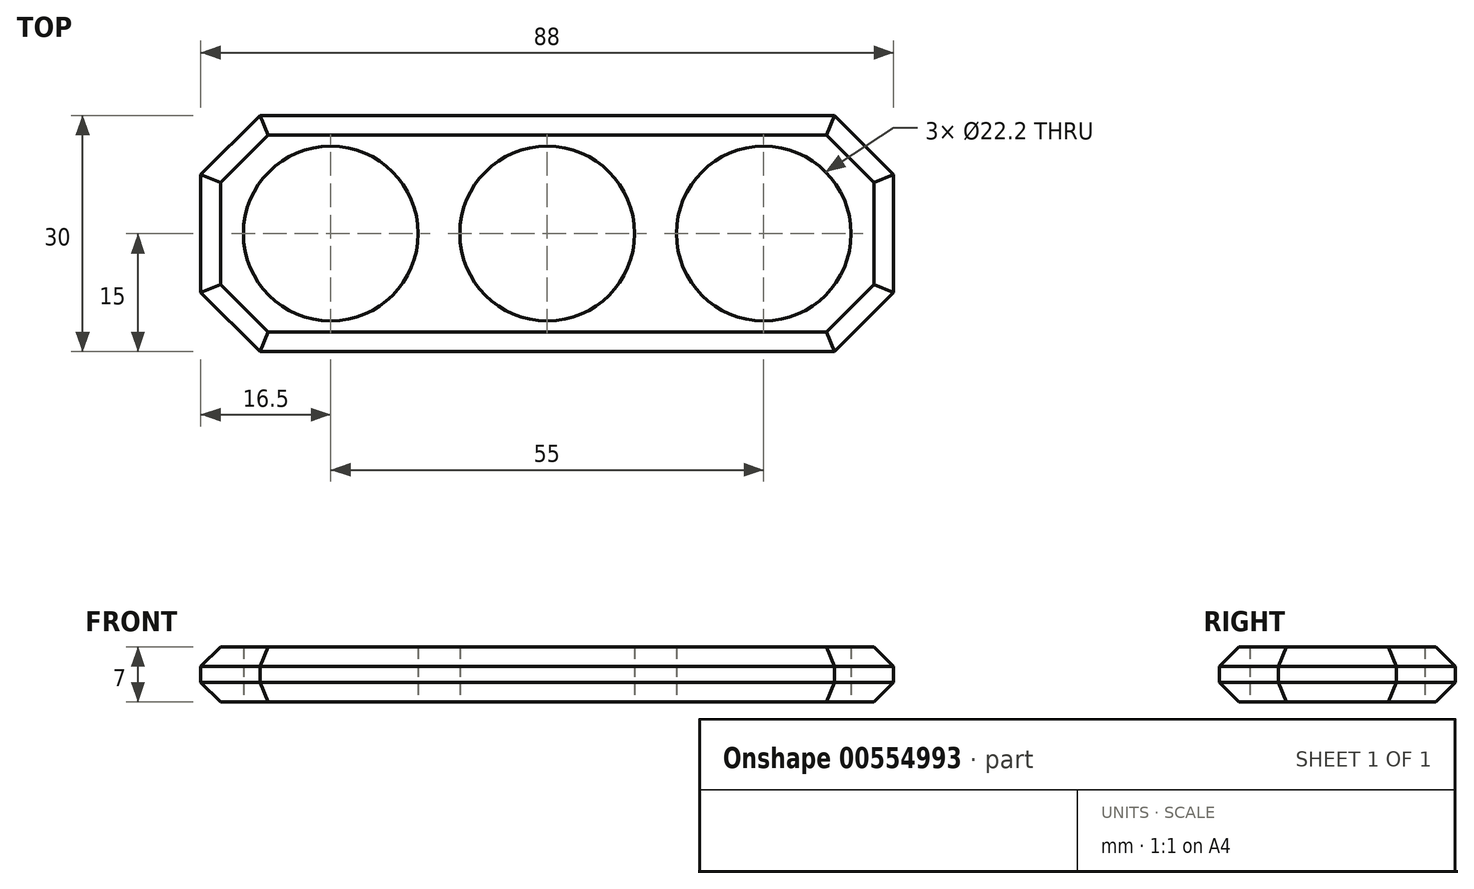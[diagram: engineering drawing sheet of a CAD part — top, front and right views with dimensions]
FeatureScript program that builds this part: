
annotation { "Feature Type Name" : "Feature", "Feature Type Description" : "" }
export const myFeature = defineFeature(function(context is Context, id is Id, definition is map)
    precondition{}
    {
        {
            var Q0;
            Q0=qCreatedBy(makeId("Top.planeOp"),FACE);
            var sketch = newSketch(context, id + "F0", { "sketchPlane" : qUnion([Q0])});
            skCircle(sketch, "E0", {"center": v(0, 0) * mm, "radius": 11.1 * mm});
            skLineSegment(sketch, "E1", {"start": v(0, 0) * mm, "end": v(27.5, 0) * mm, "construction": true});
            skCircle(sketch, "E2", {"center": v(27.5, 0) * mm, "radius": 11.1 * mm});
            skLineSegment(sketch, "E3", {"start": v(0, 0) * mm, "end": v(0, 19.82) * mm, "construction": true});
            skCircle(sketch, "E4.MirrorC", {"center": v(-27.5, 0) * mm, "radius": 11.1 * mm});
            skLineSegment(sketch, "E5.bottom", {"start": v(44, 15) * mm, "end": v(-44, 15) * mm});
            skLineSegment(sketch, "E5.top", {"start": v(44, -15) * mm, "end": v(-44, -15) * mm});
            skLineSegment(sketch, "E5.left", {"start": v(44, 15) * mm, "end": v(44, -15) * mm});
            skLineSegment(sketch, "E5.right", {"start": v(-44, 15) * mm, "end": v(-44, -15) * mm});
            skSolve(sketch);
        }
        {
            var Q0;
            Q0 = qSketchRegion(id + "F0", true);
            extrude(context, id + "F1", {"entities" : qUnion([Q0]), "depth" : 7 * mm, "offsetDistance" : 25 * mm});
        }
        {
            var Q0;
            Q0=makeQuery(id+"F1.opExtrude","SWEPT_EDGE",EDGE,{"disambiguationData":[OSD([sQuery(id+"F0.wireOp",EDGE,"E5.top"),sQuery(id+"F0.wireOp",EDGE,"E5.right")])]});
            var Q1;
            Q1=makeQuery(id+"F1.opExtrude","SWEPT_EDGE",EDGE,{"disambiguationData":[OSD([sQuery(id+"F0.wireOp",EDGE,"E5.bottom"),sQuery(id+"F0.wireOp",EDGE,"E5.right")])]});
            var Q2;
            Q2=makeQuery(id+"F1.opExtrude","SWEPT_EDGE",EDGE,{"disambiguationData":[OSD([sQuery(id+"F0.wireOp",EDGE,"E5.bottom"),sQuery(id+"F0.wireOp",EDGE,"E5.left")])]});
            var Q3;
            Q3=makeQuery(id+"F1.opExtrude","SWEPT_EDGE",EDGE,{"disambiguationData":[OSD([sQuery(id+"F0.wireOp",EDGE,"E5.top"),sQuery(id+"F0.wireOp",EDGE,"E5.left")])]});
            chamfer(context, id + "F2", {"entities" : qUnion([Q0, Q1, Q2, Q3]), "width" : 7.5 * mm, "tangentPropagation" : true});
        }
        {
            var Q0;
            Q0=makeQuery(id+"F1.opExtrude","CAP_EDGE",EDGE,{"disambiguationData":[OSD([sQuery(id+"F0.wireOp",EDGE,"E5.bottom")])],"isStart":false});
            var Q1;
            {var subQ0=sQuery(id+"F0.wireOp",EDGE,"E5.right");var subQ1=sQuery(id+"F0.wireOp",EDGE,"E5.bottom");Q1=makeQuery(id+"F2.opChamfer","BLEND_EDGE",EDGE,{"blendedFrom":[makeQuery(id+"F1.opExtrude","SWEPT_EDGE",EDGE,{"disambiguationData":[OSD([subQ1,subQ0])]}),makeQuery(id+"F1.opExtrude","CAP_FACE",FACE,{"disambiguationData":[OSD([sQuery(id+"F0.wireOp",EDGE,"E0"),sQuery(id+"F0.wireOp",EDGE,"E2"),sQuery(id+"F0.wireOp",EDGE,"E4.MirrorC"),subQ1,sQuery(id+"F0.wireOp",EDGE,"E5.top"),sQuery(id+"F0.wireOp",EDGE,"E5.left"),subQ0])],"isStart":false})],"blendedInto":[makeQuery(id+"F1.opExtrude","CAP_FACE",FACE,{"disambiguationData":[OSD([sQuery(id+"F0.wireOp",EDGE,"E0"),sQuery(id+"F0.wireOp",EDGE,"E2"),sQuery(id+"F0.wireOp",EDGE,"E4.MirrorC"),subQ1,sQuery(id+"F0.wireOp",EDGE,"E5.top"),sQuery(id+"F0.wireOp",EDGE,"E5.left"),subQ0])],"isStart":false})]});}
            var Q2;
            Q2=makeQuery(id+"F1.opExtrude","CAP_EDGE",EDGE,{"disambiguationData":[OSD([sQuery(id+"F0.wireOp",EDGE,"E5.right")])],"isStart":false});
            var Q3;
            {var subQ0=sQuery(id+"F0.wireOp",EDGE,"E5.right");var subQ1=sQuery(id+"F0.wireOp",EDGE,"E5.top");Q3=makeQuery(id+"F2.opChamfer","BLEND_EDGE",EDGE,{"blendedFrom":[makeQuery(id+"F1.opExtrude","SWEPT_EDGE",EDGE,{"disambiguationData":[OSD([subQ1,subQ0])]}),makeQuery(id+"F1.opExtrude","CAP_FACE",FACE,{"disambiguationData":[OSD([sQuery(id+"F0.wireOp",EDGE,"E0"),sQuery(id+"F0.wireOp",EDGE,"E2"),sQuery(id+"F0.wireOp",EDGE,"E4.MirrorC"),sQuery(id+"F0.wireOp",EDGE,"E5.bottom"),subQ1,sQuery(id+"F0.wireOp",EDGE,"E5.left"),subQ0])],"isStart":false})],"blendedInto":[makeQuery(id+"F1.opExtrude","CAP_FACE",FACE,{"disambiguationData":[OSD([sQuery(id+"F0.wireOp",EDGE,"E0"),sQuery(id+"F0.wireOp",EDGE,"E2"),sQuery(id+"F0.wireOp",EDGE,"E4.MirrorC"),sQuery(id+"F0.wireOp",EDGE,"E5.bottom"),subQ1,sQuery(id+"F0.wireOp",EDGE,"E5.left"),subQ0])],"isStart":false})]});}
            var Q4;
            Q4=makeQuery(id+"F1.opExtrude","CAP_EDGE",EDGE,{"disambiguationData":[OSD([sQuery(id+"F0.wireOp",EDGE,"E5.top")])],"isStart":false});
            var Q5;
            {var subQ0=sQuery(id+"F0.wireOp",EDGE,"E5.left");var subQ1=sQuery(id+"F0.wireOp",EDGE,"E5.top");Q5=makeQuery(id+"F2.opChamfer","BLEND_EDGE",EDGE,{"blendedFrom":[makeQuery(id+"F1.opExtrude","SWEPT_EDGE",EDGE,{"disambiguationData":[OSD([subQ1,subQ0])]}),makeQuery(id+"F1.opExtrude","CAP_FACE",FACE,{"disambiguationData":[OSD([sQuery(id+"F0.wireOp",EDGE,"E0"),sQuery(id+"F0.wireOp",EDGE,"E2"),sQuery(id+"F0.wireOp",EDGE,"E4.MirrorC"),sQuery(id+"F0.wireOp",EDGE,"E5.bottom"),subQ1,subQ0,sQuery(id+"F0.wireOp",EDGE,"E5.right")])],"isStart":false})],"blendedInto":[makeQuery(id+"F1.opExtrude","CAP_FACE",FACE,{"disambiguationData":[OSD([sQuery(id+"F0.wireOp",EDGE,"E0"),sQuery(id+"F0.wireOp",EDGE,"E2"),sQuery(id+"F0.wireOp",EDGE,"E4.MirrorC"),sQuery(id+"F0.wireOp",EDGE,"E5.bottom"),subQ1,subQ0,sQuery(id+"F0.wireOp",EDGE,"E5.right")])],"isStart":false})]});}
            var Q6;
            Q6=makeQuery(id+"F1.opExtrude","CAP_EDGE",EDGE,{"disambiguationData":[OSD([sQuery(id+"F0.wireOp",EDGE,"E5.left")])],"isStart":false});
            var Q7;
            {var subQ0=sQuery(id+"F0.wireOp",EDGE,"E5.left");var subQ1=sQuery(id+"F0.wireOp",EDGE,"E5.bottom");Q7=makeQuery(id+"F2.opChamfer","BLEND_EDGE",EDGE,{"blendedFrom":[makeQuery(id+"F1.opExtrude","SWEPT_EDGE",EDGE,{"disambiguationData":[OSD([subQ1,subQ0])]}),makeQuery(id+"F1.opExtrude","CAP_FACE",FACE,{"disambiguationData":[OSD([sQuery(id+"F0.wireOp",EDGE,"E0"),sQuery(id+"F0.wireOp",EDGE,"E2"),sQuery(id+"F0.wireOp",EDGE,"E4.MirrorC"),subQ1,sQuery(id+"F0.wireOp",EDGE,"E5.top"),subQ0,sQuery(id+"F0.wireOp",EDGE,"E5.right")])],"isStart":false})],"blendedInto":[makeQuery(id+"F1.opExtrude","CAP_FACE",FACE,{"disambiguationData":[OSD([sQuery(id+"F0.wireOp",EDGE,"E0"),sQuery(id+"F0.wireOp",EDGE,"E2"),sQuery(id+"F0.wireOp",EDGE,"E4.MirrorC"),subQ1,sQuery(id+"F0.wireOp",EDGE,"E5.top"),subQ0,sQuery(id+"F0.wireOp",EDGE,"E5.right")])],"isStart":false})]});}
            var Q8;
            Q8=makeQuery(id+"F1.opExtrude","CAP_EDGE",EDGE,{"disambiguationData":[OSD([sQuery(id+"F0.wireOp",EDGE,"E5.bottom")])],"isStart":true});
            var Q9;
            {var subQ0=sQuery(id+"F0.wireOp",EDGE,"E5.right");var subQ1=sQuery(id+"F0.wireOp",EDGE,"E5.bottom");Q9=makeQuery(id+"F2.opChamfer","BLEND_EDGE",EDGE,{"blendedFrom":[makeQuery(id+"F1.opExtrude","SWEPT_EDGE",EDGE,{"disambiguationData":[OSD([subQ1,subQ0])]}),makeQuery(id+"F1.opExtrude","CAP_FACE",FACE,{"disambiguationData":[OSD([sQuery(id+"F0.wireOp",EDGE,"E0"),sQuery(id+"F0.wireOp",EDGE,"E2"),sQuery(id+"F0.wireOp",EDGE,"E4.MirrorC"),subQ1,sQuery(id+"F0.wireOp",EDGE,"E5.top"),sQuery(id+"F0.wireOp",EDGE,"E5.left"),subQ0])],"isStart":true})],"blendedInto":[makeQuery(id+"F1.opExtrude","CAP_FACE",FACE,{"disambiguationData":[OSD([sQuery(id+"F0.wireOp",EDGE,"E0"),sQuery(id+"F0.wireOp",EDGE,"E2"),sQuery(id+"F0.wireOp",EDGE,"E4.MirrorC"),subQ1,sQuery(id+"F0.wireOp",EDGE,"E5.top"),sQuery(id+"F0.wireOp",EDGE,"E5.left"),subQ0])],"isStart":true})]});}
            var Q10;
            Q10=makeQuery(id+"F1.opExtrude","CAP_EDGE",EDGE,{"disambiguationData":[OSD([sQuery(id+"F0.wireOp",EDGE,"E5.right")])],"isStart":true});
            var Q11;
            {var subQ0=sQuery(id+"F0.wireOp",EDGE,"E5.right");var subQ1=sQuery(id+"F0.wireOp",EDGE,"E5.top");Q11=makeQuery(id+"F2.opChamfer","BLEND_EDGE",EDGE,{"blendedFrom":[makeQuery(id+"F1.opExtrude","SWEPT_EDGE",EDGE,{"disambiguationData":[OSD([subQ1,subQ0])]}),makeQuery(id+"F1.opExtrude","CAP_FACE",FACE,{"disambiguationData":[OSD([sQuery(id+"F0.wireOp",EDGE,"E0"),sQuery(id+"F0.wireOp",EDGE,"E2"),sQuery(id+"F0.wireOp",EDGE,"E4.MirrorC"),sQuery(id+"F0.wireOp",EDGE,"E5.bottom"),subQ1,sQuery(id+"F0.wireOp",EDGE,"E5.left"),subQ0])],"isStart":true})],"blendedInto":[makeQuery(id+"F1.opExtrude","CAP_FACE",FACE,{"disambiguationData":[OSD([sQuery(id+"F0.wireOp",EDGE,"E0"),sQuery(id+"F0.wireOp",EDGE,"E2"),sQuery(id+"F0.wireOp",EDGE,"E4.MirrorC"),sQuery(id+"F0.wireOp",EDGE,"E5.bottom"),subQ1,sQuery(id+"F0.wireOp",EDGE,"E5.left"),subQ0])],"isStart":true})]});}
            var Q12;
            Q12=makeQuery(id+"F1.opExtrude","CAP_EDGE",EDGE,{"disambiguationData":[OSD([sQuery(id+"F0.wireOp",EDGE,"E5.top")])],"isStart":true});
            var Q13;
            {var subQ0=sQuery(id+"F0.wireOp",EDGE,"E5.left");var subQ1=sQuery(id+"F0.wireOp",EDGE,"E5.top");Q13=makeQuery(id+"F2.opChamfer","BLEND_EDGE",EDGE,{"blendedFrom":[makeQuery(id+"F1.opExtrude","SWEPT_EDGE",EDGE,{"disambiguationData":[OSD([subQ1,subQ0])]}),makeQuery(id+"F1.opExtrude","CAP_FACE",FACE,{"disambiguationData":[OSD([sQuery(id+"F0.wireOp",EDGE,"E0"),sQuery(id+"F0.wireOp",EDGE,"E2"),sQuery(id+"F0.wireOp",EDGE,"E4.MirrorC"),sQuery(id+"F0.wireOp",EDGE,"E5.bottom"),subQ1,subQ0,sQuery(id+"F0.wireOp",EDGE,"E5.right")])],"isStart":true})],"blendedInto":[makeQuery(id+"F1.opExtrude","CAP_FACE",FACE,{"disambiguationData":[OSD([sQuery(id+"F0.wireOp",EDGE,"E0"),sQuery(id+"F0.wireOp",EDGE,"E2"),sQuery(id+"F0.wireOp",EDGE,"E4.MirrorC"),sQuery(id+"F0.wireOp",EDGE,"E5.bottom"),subQ1,subQ0,sQuery(id+"F0.wireOp",EDGE,"E5.right")])],"isStart":true})]});}
            var Q14;
            Q14=makeQuery(id+"F1.opExtrude","CAP_EDGE",EDGE,{"disambiguationData":[OSD([sQuery(id+"F0.wireOp",EDGE,"E5.left")])],"isStart":true});
            var Q15;
            {var subQ0=sQuery(id+"F0.wireOp",EDGE,"E5.left");var subQ1=sQuery(id+"F0.wireOp",EDGE,"E5.bottom");Q15=makeQuery(id+"F2.opChamfer","BLEND_EDGE",EDGE,{"blendedFrom":[makeQuery(id+"F1.opExtrude","SWEPT_EDGE",EDGE,{"disambiguationData":[OSD([subQ1,subQ0])]}),makeQuery(id+"F1.opExtrude","CAP_FACE",FACE,{"disambiguationData":[OSD([sQuery(id+"F0.wireOp",EDGE,"E0"),sQuery(id+"F0.wireOp",EDGE,"E2"),sQuery(id+"F0.wireOp",EDGE,"E4.MirrorC"),subQ1,sQuery(id+"F0.wireOp",EDGE,"E5.top"),subQ0,sQuery(id+"F0.wireOp",EDGE,"E5.right")])],"isStart":true})],"blendedInto":[makeQuery(id+"F1.opExtrude","CAP_FACE",FACE,{"disambiguationData":[OSD([sQuery(id+"F0.wireOp",EDGE,"E0"),sQuery(id+"F0.wireOp",EDGE,"E2"),sQuery(id+"F0.wireOp",EDGE,"E4.MirrorC"),subQ1,sQuery(id+"F0.wireOp",EDGE,"E5.top"),subQ0,sQuery(id+"F0.wireOp",EDGE,"E5.right")])],"isStart":true})]});}
            chamfer(context, id + "F3", {"entities" : qUnion([Q0, Q1, Q2, Q3, Q4, Q5, Q6, Q7, Q8, Q9, Q10, Q11, Q12, Q13, Q14, Q15]), "width" : 2.5 * mm, "tangentPropagation" : true});
        }
    });
